# Revit family: 456
name_source: partatom
category: Pipe Accessories
revit_build: Autodesk Revit 2018 (Build: 20170223_1515(x64)
units: mm (PartAtom-declared; Revit-internal decimal feet)

## family parameters
Always vertical = No
Cut with Voids When Loaded = No
OmniClass Number = 23.27.43.00
Part Type = Valve - Breaks Into
Round Connector Dimension = Use Diameter
Shared = No
Work Plane-Based = Yes

## types (4) — shared parameters
Apparent Load = 0 VA
Assembly Code = D2040100
BIMobject category = Valves
D = 30 mm  [stored 0.0984252 ft]
DD = 21.8 mm  [stored 0.0715223 ft]
Default Elevation = 1219.2 mm  [stored 4 ft]
Description = 30-36 Mm Connector
Design country = Italy
Dimensions = 30-36
Edition number = 1
H = 27.5 mm
IFC Classification = Pipe Fitting
Keynote = 15410
L1 = 7 mm  [stored 0.0229659 ft]
Manufacturer = Aignep Spa
Manufacturer country = Italy
Manufacturer name = Aignep Spa
Material main = Brass
Number of Poles = 1
OmniClass Code = 23-27 43 00
OmniClass Description = Pipe Fittings
Power Factor = 1
Product Guid = 2e037b33-d9ea-47d4-863b-0ab0419701fb
Product SKU = 30-36-Mm-Connector-Connector-30-36
Product certification = https://www.aignep.com
Product data url = https://www.bimobject.com
Product family = INFINITY
Product group = Valves
Product name = 30-36 Mm Connector - Connector 30-36
Product url = https://www.aignep.com
QR code = https://www.bimobject.com
Secondary Material = AIGNEP - Plastic - Black
URL = https://www.aignep.com
W = 40.9 mm
W1 = 27.5 mm

## per-type parameters (varying)
| type | Product Material | Specification | Voltage |
| CON31 000 01 | AIGNEP - Plastic - Black | 2 PINS | 0 V |
| CON32 024 00 | AIGNEP - Plastic - Transparent | LED + VDR 0 - 24V | 24 V |
| CON32 110 00 | AIGNEP - Plastic - Transparent | LED + VDR 110V | 110 V |
| CON32 250 00 | AIGNEP - Plastic - Transparent | LED + VDR 220V | 220 V |

note: column(s) folded — value = type name in every type: Model

note: [stored X ft] marks values corroborated as IEEE doubles in the binary element streams (Revit-internal decimal feet)

## geometry (parser evidence)
native form markers: Sweep x1
no freeform markers — native parametric forms only
